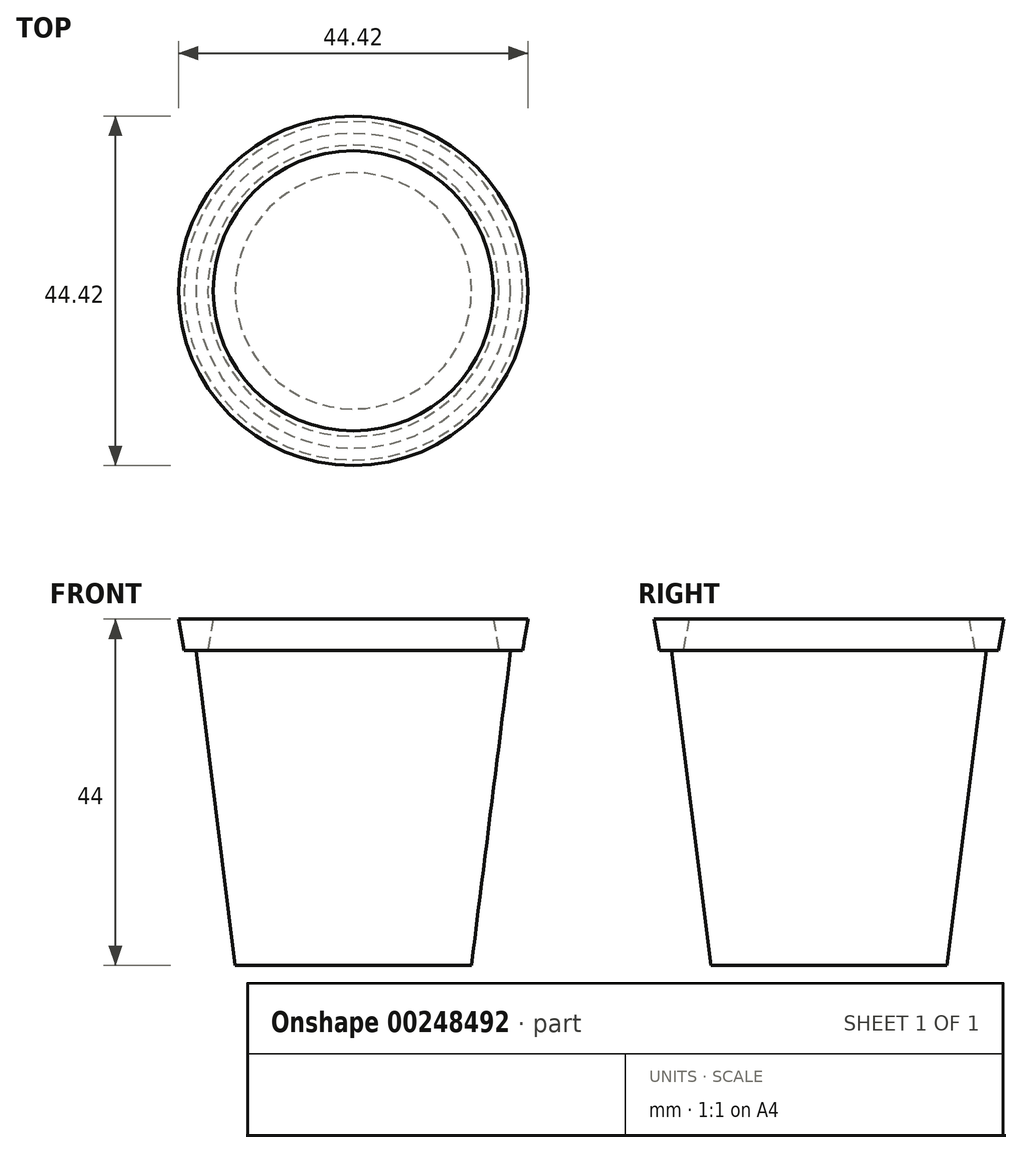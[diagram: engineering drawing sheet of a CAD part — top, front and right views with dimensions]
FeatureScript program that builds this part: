
annotation { "Feature Type Name" : "Feature", "Feature Type Description" : "" }
export const myFeature = defineFeature(function(context is Context, id is Id, definition is map)
    precondition{}
    {
        {
            var Q0;
            Q0=qCreatedBy(makeId("Top.planeOp"),FACE);
            var sketch = newSketch(context, id + "F0", { "sketchPlane" : qUnion([Q0])});
            skCircle(sketch, "E0", {"center": v(0, 0) * mm, "radius": 15 * mm});
            skSolve(sketch);
        }
        {
            var Q0;
            Q0=qCreatedBy(makeId("Top.planeOp"),FACE);
            cPlane(context, id + "F1", {"entities" : qUnion([Q0]), "cplaneType" : CPlaneType.OFFSET, "offset" : 40 * mm, "width" : 150 * mm, "height" : 150 * mm});
        }
        {
            var Q0;
            Q0=qCreatedBy(id+"F1.planeOp",FACE);
            var sketch = newSketch(context, id + "F2", { "sketchPlane" : qUnion([Q0])});
            skCircle(sketch, "E1", {"center": v(0, 0) * mm, "radius": 20 * mm});
            skSolve(sketch);
        }
        {
            var Q0;
            Q0=makeQuery(id+"F0.imprint","IMPRINT",FACE,{"disambiguationData":[TD([[makeQuery(id+"F0.imprint","IMPRINT",EDGE,{"derivedFrom":sQuery(id+"F0.wireOp",EDGE,"E0")}),1.0]])]});
            var Q1;
            Q1=makeQuery(id+"F2.imprint","IMPRINT",FACE,{"disambiguationData":[TD([[makeQuery(id+"F2.imprint","IMPRINT",EDGE,{"derivedFrom":sQuery(id+"F2.wireOp",EDGE,"E1")}),1.0]])]});
            loft(context, id + "F3", {"sheetProfilesArray" : [{ "sheetProfileEntities" : qUnion([Q0]) }, { "sheetProfileEntities" : qUnion([Q1]) }]});
        }
        {
            var Q0;
            Q0=makeQuery(id+"F3.opLoft","CAP_FACE",FACE,{"disambiguationData":[OSD([makeQuery(id+"F2.imprint","IMPRINT",FACE,{"disambiguationData":[TD([[makeQuery(id+"F2.imprint","IMPRINT",EDGE,{"derivedFrom":sQuery(id+"F2.wireOp",EDGE,"E1")}),1.0]])]})])],"isStart":true});
            var sketch = newSketch(context, id + "F4", { "sketchPlane" : qUnion([Q0])});
            skCircle(sketch, "E2", {"center": v(0, 0) * mm, "radius": 21.5 * mm});
            skCircle(sketch, "E3", {"center": v(0, 0) * mm, "radius": 18.5 * mm});
            skSolve(sketch);
        }
        {
            var Q0;
            Q0=makeQuery(id+"F4.imprint","IMPRINT",FACE,{"disambiguationData":[TD([[makeQuery(id+"F4.imprint","IMPRINT",EDGE,{"derivedFrom":sQuery(id+"F4.wireOp",EDGE,"E2")}),1.0]])]});
            var Q1;
            Q1=makeQuery(id+"F4.imprint","IMPRINT",FACE,{"disambiguationData":[TD([[makeQuery(id+"F4.imprint","IMPRINT",EDGE,{"derivedFrom":sQuery(id+"F4.wireOp",EDGE,"E3")}),-1.0]])]});
            extrude(context, id + "F5", {"entities" : qUnion([Q0, Q1]), "operationType" : NewBodyOperationType.ADD, "depth" : 4 * mm, "hasDraft" : true, "draftAngle" : 10 * degree});
        }
    });
